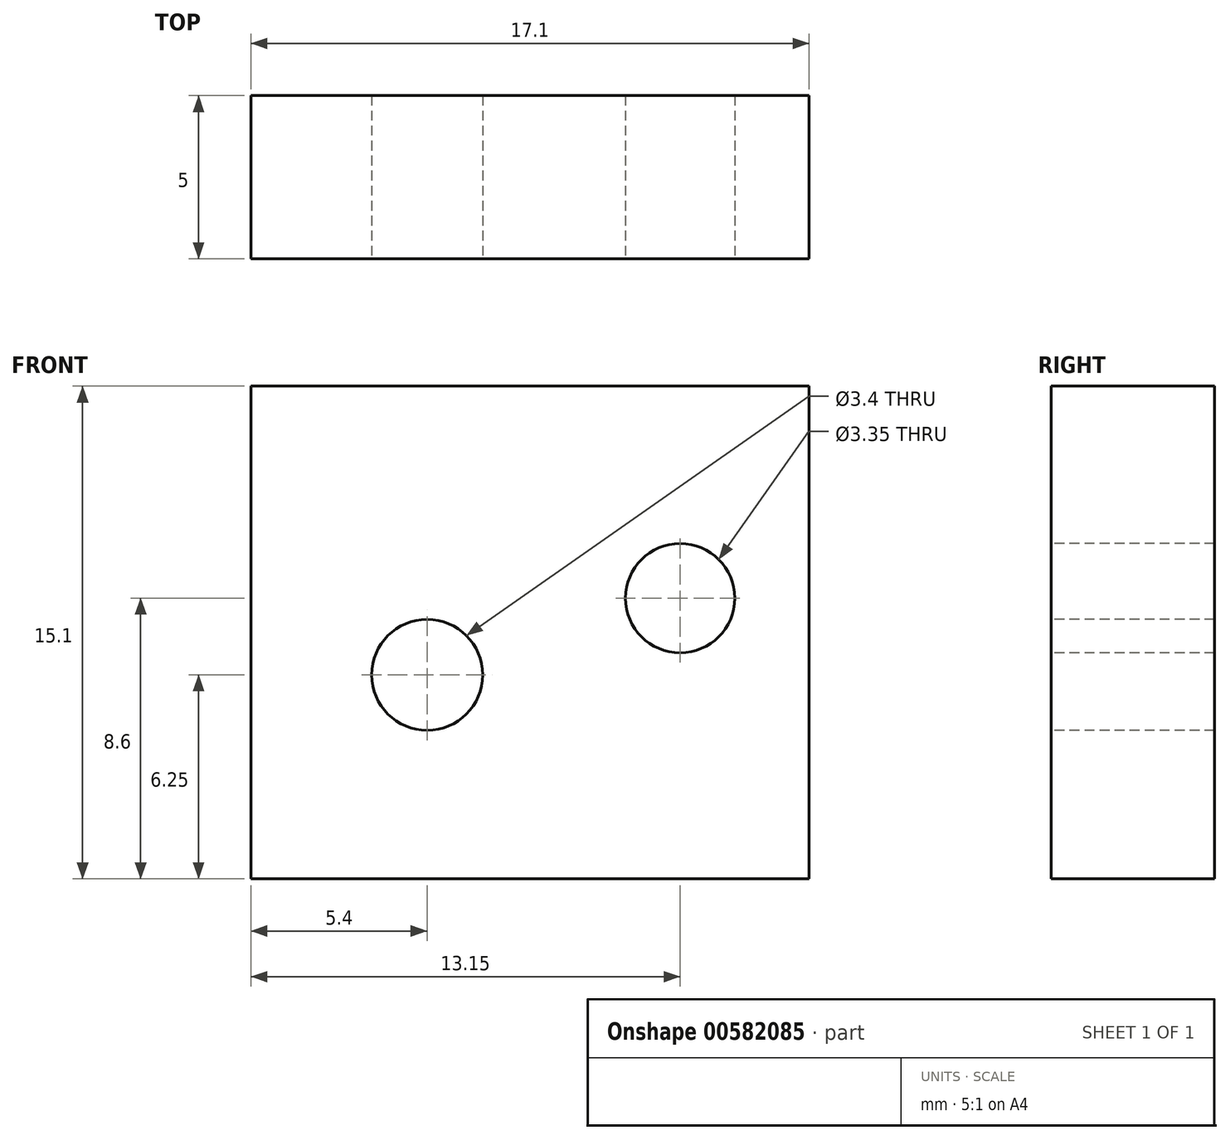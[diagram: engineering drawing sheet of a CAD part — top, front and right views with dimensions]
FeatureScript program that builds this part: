
annotation { "Feature Type Name" : "Feature", "Feature Type Description" : "" }
export const myFeature = defineFeature(function(context is Context, id is Id, definition is map)
    precondition{}
    {
        {
            var Q0;
            Q0=qCreatedBy(makeId("Front.planeOp"),FACE);
            var sketch = newSketch(context, id + "F0", { "sketchPlane" : qUnion([Q0])});
            skLineSegment(sketch, "E0.bottom", {"start": v(8.55, 7.55) * mm, "end": v(-8.55, 7.55) * mm});
            skLineSegment(sketch, "E0.top", {"start": v(8.55, -7.55) * mm, "end": v(-8.55, -7.55) * mm});
            skLineSegment(sketch, "E0.left", {"start": v(8.55, 7.55) * mm, "end": v(8.55, -7.55) * mm});
            skLineSegment(sketch, "E0.right", {"start": v(-8.55, 7.55) * mm, "end": v(-8.55, -7.55) * mm});
            skPoint(sketch, "E0.middle", {"position": v(0, 0) * mm});
            skSolve(sketch);
        }
        {
            var Q0;
            Q0=makeQuery(id+"F0.imprint","IMPRINT",FACE,{"disambiguationData":[TD([[makeQuery(id+"F0.imprint","IMPRINT",EDGE,{"derivedFrom":sQuery(id+"F0.wireOp",EDGE,"E0.bottom")}),1.0]])]});
            extrude(context, id + "F1", {"entities" : qUnion([Q0]), "depth" : 5 * mm, "offsetDistance" : 25 * mm});
        }
        {
            var Q0;
            Q0=makeQuery(id+"F1.opExtrude","CAP_FACE",FACE,{"disambiguationData":[OSD([sQuery(id+"F0.wireOp",EDGE,"E0.bottom"),sQuery(id+"F0.wireOp",EDGE,"E0.top"),sQuery(id+"F0.wireOp",EDGE,"E0.left"),sQuery(id+"F0.wireOp",EDGE,"E0.right")])],"isStart":false});
            var sketch = newSketch(context, id + "F2", { "sketchPlane" : qUnion([Q0])});
            skCircle(sketch, "E1", {"center": v(-3.15, -1.3) * mm, "radius": 1.7 * mm});
            skCircle(sketch, "E2", {"center": v(4.6, 1.05) * mm, "radius": 1.68 * mm});
            skSolve(sketch);
        }
        {
            var Q0;
            Q0=makeQuery(id+"F2.imprint","IMPRINT",FACE,{"disambiguationData":[TD([[makeQuery(id+"F2.imprint","IMPRINT",EDGE,{"derivedFrom":sQuery(id+"F2.wireOp",EDGE,"E2")}),1.0]])]});
            var Q1;
            Q1=makeQuery(id+"F2.imprint","IMPRINT",FACE,{"disambiguationData":[TD([[makeQuery(id+"F2.imprint","IMPRINT",EDGE,{"derivedFrom":sQuery(id+"F2.wireOp",EDGE,"E1")}),1.0]])]});
            extrude(context, id + "F3", {"entities" : qUnion([Q0, Q1]), "operationType" : NewBodyOperationType.REMOVE, "oppositeDirection" : true, "depth" : 25 * mm, "offsetDistance" : 25 * mm});
        }
    });
